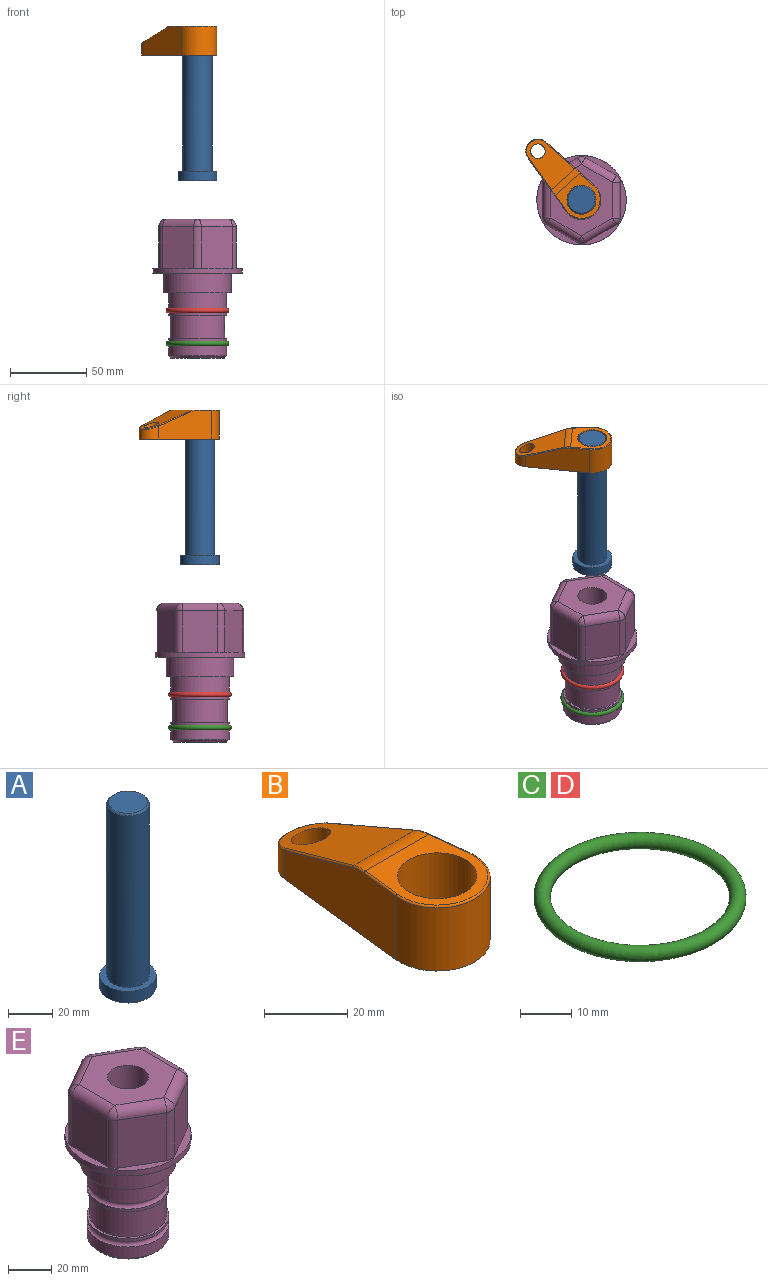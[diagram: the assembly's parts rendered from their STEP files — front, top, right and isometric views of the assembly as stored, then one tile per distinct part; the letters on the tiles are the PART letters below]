
ASSEMBLY  parts=5 mates=3
PART A: 6 faces, bbox 25.4x25.4x101.6 mm
  f0: plane 17.46x17.46mm, normal (0,0,1), area 239.5mm2, adj f5
  f1: plane 25.4x25.4mm, normal (0,0,-1), area 506.7mm2, adj f2
  f2: cylinder r=12.7mm len=25.4mm, axis (0,0,1), area 506.7mm2, adj f1,f3
  f3: plane 25.4x25.4mm, normal (0,0,1), area 221.7mm2, adj f2,f4
  f4: cylinder r=9.53mm len=94.46mm, axis (0,0,1), area 5653mm2, adj f3,f5
  f5: cone r=8.73mm half-angle=45deg, axis (0,0,-1), area 64.4mm2, adj f0,f4
PART B: 44 faces, bbox 27.5x64.5x19.1 mm
  f0: plane 2.3x0.95mm, normal (0,0,-1), area 1mm2, adj f25,f30,f34
  f1: plane 63.5x25.4mm, normal (0,0,-1), area 561.7mm2, adj f2,f3,f4,f5,f6,f7,f19,f20
  f2: cylinder r=12.7mm len=25.4mm, axis (0,0,-1), area 792.2mm2, adj f1,f3,f5,f13
  f3: plane 42.33x18.54mm, normal (0.99,0.11,0), area 647mm2, adj f1,f2,f4,f11,f12,f14
  f4: cylinder r=7.94mm len=15.78mm, axis (0,0,-1), area 158.6mm2, adj f1,f3,f5,f16
  f5: plane 42.33x18.54mm, normal (-0.99,0.11,0), area 647mm2, adj f1,f2,f4,f15,f17,f18
  f6: cylinder r=9.53mm len=19.05mm, axis (0,0,-1), area 1140.1mm2, adj f1,f8
  f7: cylinder r=4.76mm len=10.98mm, axis (0,0,-1), area 276.1mm2, adj f1,f9
  f8: plane 25.83x24.38mm, normal (0,0,1), area 262.2mm2, adj f6,f10,f11,f13,f15
  f9: plane 32.49x20.55mm, normal (0,0.34,0.94), area 489.9mm2, adj f7,f10,f14,f16,f18
  f10: cylinder r=12.7mm len=21.49mm, axis (-1,0,0), area 93.2mm2, adj f8,f9,f12,f17
  f11: cylinder r=0.51mm len=12.34mm, axis (0.11,-0.99,0), area 9.9mm2, adj f3,f8,f12,f13
  f12: bspline ~7.62x1.64mm, area 3.5mm2, adj f3,f10,f11,f14
  f13: torus R=12.19mm, axis (0,0,1), area 33.6mm2, adj f2,f8,f11,f15
  f14: cylinder r=0.51mm len=26.01mm, axis (0.1,-0.93,0.34), area 21.6mm2, adj f3,f9,f12,f16
  f15: cylinder r=0.51mm len=12.34mm, axis (0.11,0.99,0), area 9.9mm2, adj f5,f8,f13,f17
  f16: bspline ~15.78x7.05mm, area 15.7mm2, adj f4,f9,f14,f18
  f17: bspline ~7.62x1.64mm, area 3.5mm2, adj f5,f10,f15,f18
  f18: cylinder r=0.51mm len=26.01mm, axis (0.1,0.93,-0.34), area 21.6mm2, adj f5,f9,f16,f17
  f19: plane 21.6x14.29mm, normal (-0.99,-0.11,0), area 242.6mm2, adj f1,f26,f28,f34,f36,f38
  f20: plane 21.6x14.29mm, normal (0.99,-0.11,0), area 242.6mm2, adj f1,f27,f29,f37,f39,f41
  f21: cylinder r=12.7mm len=14.29mm, axis (0,0,-1), area 173.2mm2, adj f1,f26,f27,f30,f31,f33
  f22: cylinder r=7.94mm len=7.63mm, axis (0,0,-1), area 53.8mm2, adj f1,f28,f29,f42
  f23: plane 2.3x0.95mm, normal (0,0,-1), area 1mm2, adj f25,f33,f37
  f24: plane 17.94x12.32mm, normal (0,-0.34,-0.94), area 191.2mm2, adj f25,f38,f41,f42
  f25: cylinder r=9.53mm len=12.93mm, axis (-1,0,0), area 37.5mm2, adj f0,f23,f24,f31,f36,f39
  f26: cylinder r=1.59mm len=14.29mm, axis (0,0,-1), area 49mm2, adj f1,f19,f21,f32
  f27: cylinder r=1.59mm len=14.29mm, axis (0,0,-1), area 49mm2, adj f1,f20,f21,f35
  f28: cylinder r=1.59mm len=7.28mm, axis (0,0,-1), area 22.1mm2, adj f1,f19,f22,f40
  f29: cylinder r=1.59mm len=7.28mm, axis (0,0,-1), area 22.1mm2, adj f1,f20,f22,f43
  f30: torus R=14.29mm, axis (0,0,1), area 5.8mm2, adj f0,f21,f31,f32
  f31: bspline ~11.06x2.73mm, area 20.8mm2, adj f21,f25,f30,f33
  f32: sphere r=1.59mm, area 5.4mm2, adj f26,f30,f34
  f33: torus R=14.29mm, axis (0,0,1), area 5.8mm2, adj f21,f23,f31,f35
  f34: cylinder r=1.59mm len=1.68mm, axis (-0.11,0.99,0), area 2.4mm2, adj f0,f19,f32,f36
  f35: sphere r=1.59mm, area 5.4mm2, adj f27,f33,f37
  f36: bspline ~5.82x2.33mm, area 7.7mm2, adj f19,f25,f34,f38
  f37: cylinder r=1.59mm len=1.68mm, axis (0.11,0.99,0), area 2.4mm2, adj f20,f23,f35,f39
  f38: cylinder r=1.59mm len=18.33mm, axis (0.1,-0.93,0.34), area 46.7mm2, adj f19,f24,f36,f40
  f39: bspline ~5.82x2.33mm, area 7.7mm2, adj f20,f25,f37,f41
  f40: sphere r=1.59mm, area 3.6mm2, adj f28,f38,f42
  f41: cylinder r=1.59mm len=18.33mm, axis (0.1,0.93,-0.34), area 46.7mm2, adj f20,f24,f39,f43
  f42: bspline ~8.31x1.84mm, area 15.3mm2, adj f22,f24,f40,f43
  f43: sphere r=1.59mm, area 3.6mm2, adj f29,f41,f42
PART C: 1 faces, bbox 44.7x44.7x3.2 mm
  f0: torus R=19.05mm, axis (0,0,1), area 1193.9mm2
PART D: same geometry as C
PART E: 47 faces, bbox 58.7x58.7x91.2 mm
  f0: cylinder r=17.78mm len=35.56mm, axis (0,0,1), area 1670.8mm2, adj f22,f23,f30
  f1: cylinder r=19.05mm len=38.1mm, axis (0,0,1), area 1191.9mm2, adj f25,f26,f29
  f2: plane 58.66x58.66mm, normal (0,0,-1), area 1150.6mm2, adj f3,f27
  f3: cylinder r=29.33mm len=58.66mm, axis (0,0,-1), area 585.1mm2, adj f2,f4
  f4: plane 58.66x58.66mm, normal (0,0,1), area 475.9mm2, adj f3,f6,f7,f8,f9,f10,f11,f12
  f5: plane 46.93x40.64mm, normal (0,0,1), area 1145.3mm2, adj f34,f35,f38,f39,f42,f43,f46
  f6: plane 27.31x20.32mm, normal (-0.5,0.87,0), area 640.7mm2, adj f4,f16,f17,f42
  f7: plane 27.31x20.32mm, normal (0.5,0.87,0), area 640.7mm2, adj f4,f15,f16,f46
  f8: plane 27.31x23.46mm, normal (1,0,0), area 640.7mm2, adj f4,f14,f15,f43
  f9: plane 27.31x20.32mm, normal (0.5,-0.87,0), area 640.7mm2, adj f4,f13,f14,f39
  f10: plane 27.31x20.32mm, normal (-0.5,-0.87,0), area 640.7mm2, adj f4,f12,f13,f35
  f11: plane 27.31x23.46mm, normal (-1,0,0), area 640.7mm2, adj f4,f12,f17,f38
  f12: cylinder r=5.08mm len=27.31mm, axis (0,0,-1), area 145.3mm2, adj f4,f10,f11,f36
  f13: cylinder r=5.08mm len=27.31mm, axis (0,0,-1), area 145.3mm2, adj f4,f9,f10,f37
  f14: cylinder r=5.08mm len=27.31mm, axis (0,0,-1), area 145.3mm2, adj f4,f8,f9,f41
  f15: cylinder r=5.08mm len=27.31mm, axis (0,0,-1), area 145.3mm2, adj f4,f7,f8,f45
  f16: cylinder r=5.08mm len=27.31mm, axis (0,0,-1), area 145.3mm2, adj f4,f6,f7,f44
  f17: cylinder r=5.08mm len=27.31mm, axis (0,0,-1), area 145.3mm2, adj f4,f6,f11,f40
  f18: plane 34.93x34.93mm, normal (0,0,-1), area 958mm2, adj f28
  f19: cylinder r=19.05mm len=38.1mm, axis (0,0,1), area 760.1mm2, adj f20,f28
  f20: torus R=19.05mm, axis (0,0,1), area 565.3mm2, adj f19,f21
  f21: cylinder r=19.05mm len=38.1mm, axis (0,0,1), area 190mm2, adj f20,f22
  f22: plane 38.1x38.1mm, normal (0,0,1), area 146.9mm2, adj f0,f21
  f23: plane 38.1x38.1mm, normal (0,0,-1), area 146.9mm2, adj f0,f24
  f24: cylinder r=19.05mm len=38.1mm, axis (0,0,1), area 190mm2, adj f23,f25
  f25: torus R=19.05mm, axis (0,0,1), area 565.3mm2, adj f1,f24
  f26: plane 44.45x44.45mm, normal (0,0,-1), area 411.7mm2, adj f1,f27
  f27: cylinder r=22.23mm len=44.45mm, axis (0,0,1), area 1773.5mm2, adj f2,f26
  f28: cone r=19.05mm half-angle=45deg, axis (0,0,1), area 257.5mm2, adj f18,f19
  f29: cylinder r=3.17mm len=6.75mm, axis (-1,0,0), area 128mm2, adj f1,f32
  f30: cylinder r=3.17mm len=6.35mm, axis (-1,0,0), area 102.5mm2, adj f0,f32
  f31: plane 25.4x25.4mm, normal (0,0,1), area 506.7mm2, adj f32
  f32: cylinder r=12.7mm len=66.42mm, axis (0,0,-1), area 5236.2mm2, adj f29,f30,f31,f33
  f33: cone r=9.53mm half-angle=30deg, axis (0,0,-1), area 443.4mm2, adj f32,f34
  f34: cylinder r=9.53mm len=19.05mm, axis (0,0,-1), area 849mm2, adj f5,f33
  f35: cylinder r=5.08mm len=22.86mm, axis (-0.87,0.5,0), area 187.2mm2, adj f5,f10,f36,f37
  f36: sphere r=5.08mm, area 27mm2, adj f12,f35,f38
  f37: sphere r=5.08mm, area 27mm2, adj f13,f35,f39
  f38: cylinder r=5.08mm len=23.46mm, axis (0,1,0), area 187.2mm2, adj f5,f11,f36,f40
  f39: cylinder r=5.08mm len=22.86mm, axis (-0.87,-0.5,0), area 187.2mm2, adj f5,f9,f37,f41
  f40: sphere r=5.08mm, area 27mm2, adj f17,f38,f42
  f41: sphere r=5.08mm, area 27mm2, adj f14,f39,f43
  f42: cylinder r=5.08mm len=22.86mm, axis (0.87,0.5,0), area 187.2mm2, adj f5,f6,f40,f44
  f43: cylinder r=5.08mm len=23.46mm, axis (0,-1,0), area 187.2mm2, adj f5,f8,f41,f45
  f44: sphere r=5.08mm, area 27mm2, adj f16,f42,f46
  f45: sphere r=5.08mm, area 27mm2, adj f15,f43,f46
  f46: cylinder r=5.08mm len=22.86mm, axis (0.87,-0.5,0), area 187.2mm2, adj f5,f7,f44,f45
PLACE A rot(axis=(0,0,1),131.9deg) t=(-22.12,-10.56,69.4)mm
PLACE B rot(axis=(0,0,1),41.9deg) t=(-22.12,-10.56,124.01)mm
PLACE C t=(-22.12,-10.56,-40.73)mm
PLACE D t=(-22.12,-10.56,-19.14)mm
PLACE E t=(-22.12,-10.56,-19.14)mm fixed
MATE fastened C.f0 <-> E.f0  axis (0,0,1) through (-22.12,-10.56,-65.24)mm
MATE cylindrical A.f2 <-> E.f0  axis (0,0,1) through (-22.12,-10.56,95.04)mm
MATE fastened B.f2 <-> A.f2  axis (0,0,1) through (-22.12,-10.56,143.06)mm
